# Revit family: ONIZ_5BF
name_source: partatom
category: Mechanical Equipment
units: mm (PartAtom-declared; Revit-internal decimal feet)

## family parameters
Always vertical = Yes
Cut with Voids When Loaded = No
OmniClass Number = 23.40.40.11.17
OmniClass Title = Refrigerated Cases
Part Type = Normal
Room Calculation Point = No
Round Connector Dimension = Use Radius
Shared = No
Work Plane-Based = Yes

## types (4) — shared parameters
BASE HEIGHT = 5"
CERTIFICATIONS = NSF 7, UL471, CSA
COIL REFRIGERATION CHARGE = 0.00 lb
CONTROL TYPE = T-STAT
DATE = 03/15/12
DEDICATED CIRCUIT = YES
DEFROST PHASE = 1
DEFROST TIME AND DURATION = 2 @ 60 MIN
DEFROST WATTAGE = 0 W
DIEBOARD HEIGHT = 0"
DISCHARGE AIR TEMPERATURE = 0 °F
DRAIN LINE CONNECTION = Drain Connection
DRAIN LINE DIAMETER = 2"
DRAIN LINE RADIUS = 1"
DRAIN PIPE LENGTH = 0"
DRAIN PIPE TYPE = PVC
DRIP PAN PLUMB TYPE = HARD
Default Elevation = 48"
Description = Narrow Single-Deck Island Merchandiser
ELECTRIC DEFROST = No
ELECTRICAL DEFROST VOLTAGE = 0 V
EQUIPMENT MARK = ONIZ
EVAPORATOR TEMPERATURE = 0 °F
FAN CONNECTOR DESCRIPTION = FAN AND ANTI SWEAT CONNECTOR
FAN NUMBER OF POLES = 1
FAN TYPE = ECM
FROZEN CASE = Yes
GROUND FAULT PROTECTION = NO
HEIGHT = 34 15/16"
HOT GAS DEFROST = No
ISOLATED GROUND REQUIRED = NO
Keynote = Frozen Food/ Ice Cream
LED LIGHTING AMPS = 0 A
LED LIGHTING AMPS PER ROW = 0 A
LED LIGHTING WATTAGE = 0 W
LIGHT AMPS = 0 A
LIGHT TYPE = T8 FLUORESCENT
LIGHTING APPARENT LOAD = 0 VA
LIGHTING CONNECTION DESCRIPTION = LIGHTING CONNECTOR
LIGHTING NUMBER OF POLES = 1
LIGHTING WATTAGE = 0 VA
LIQUID LINE CONNECTION = LIQUID LINE CONNECTION
LIQUID LINE DIAMETER = 0"
LIQUID LINE RADIUS = 0"
Manufacturer = HILL PHOENIX
NUMBER OF WIRES = 3
PHASE = 1
POWER FACTOR = 1
PRESSURE REGULATOR = 0.00 psi
RECEPTICAL MOUNTING HEIGHT ABOVE FLOOR = 19 3/4"
REF PLANE FRONT BACK = 22 1/2"
REVERSE AIR DEFROST = No
SET BACK MODE FOR ENERGY CONSERVATION = NO
SHELVE LENGTH = 48"
SIZE OF COLD WATER HOOK UP = 0"
SIZE OF HOT WATER HOOK-UP = 0"
SUCTION LINE CONNECTION = SUCTION LINE CONNECTION
SUCTION LINE DIAMETER = 1"
SUCTION LINE RADIUS = 0"
T8 LIGHT OR LED LIGHT = Yes
T8 LIGHTING AMPS = 0 A
T8 LIGHTING AMPS PER ROW = 0 A
T8 LIGHTING WATTAGE = 0 W
TIME OFF DEFROST = Yes
TOEKICK HEIGHT = 5 1/2"
TOEKICK INSET = 1 1/2"
URL = http://www.hillphoenix.com
VOLTAGE = 120 V
WATER LINE MOUNTING HEIGHT ABOVE FLOOR = 0"
WEIGHT = 0.00 lb
WIDTH = 45"
zero-valued in all types: BTU ADD FOR LIGHTS, BTU ADD PER SHELF PER FOOT, BTU PER FOOT CONVENTIONAL, BTU PER FOOT PARALLEL, CONVENTIONAL EVAPORATOR LOAD, CORNICE AND NOSE LIGHT ROWS, LED LIGHTING BTU ADD PER ROW, PARALLEL EVAPORATOR LOAD, SHELF LIGHT ROWS, T8 LIGHTING BTU ADD PER ROW

## per-type parameters (varying)
| type | ANTI SWEAT APPARENT LOAD | ANTI SWEAT HEATER AMPS | ANTI SWEAT HEATER WATTAGE | C CASE DEFROST AMPS | DEFROST AMPS | F CASE DEFROST AMPS | FAN AMPS | FAN AND ANTI SWEAT HEATER APPARENT LOAD | FAN APPARENT LOAD | FAN QUANTITY | FAN WATTAGE | LENGTH | LENGTH FOR BTU | REF PLANE LEFT RIGHT | TOTAL APPARENT FAN-LIGHT AND A/S LOAD | TOTAL CASE AMPS | TOTAL CASE WATTAGE |
| ONIZ-8' | 157 VA | 1 A | 157 W | 15 A | 8 A | 8 A | 0 A | 211 VA | 54 VA | 3 | 33 W | 96" | 8 | 48" | 190 VA | 2 A | 190 W |
| ONIZ-12' | 238 VA | 2 A | 238 W | 23 A | 12 A | 12 A | 1 A | 310 VA | 72 VA | 4 | 44 W | 144" | 12 | 72" | 282 VA | 3 A | 282 W |
| ONIZ-6' | 134 VA | 1 A | 134 W | 12 A | 6 A | 6 A | 0 A | 170 VA | 36 VA | 2 | 22 W | 72" | 6 | 36" | 156 VA | 1 A | 156 W |
| ONIZ-10' | 192 VA | 2 A | 192 W | 16 A | 10 A | 10 A | 0 A | 246 VA | 54 VA | 3 | 33 W | 120" | 10 | 60" | 225 VA | 2 A | 225 W |

note: column(s) folded — value = type name in every type: LEGEND NUMBER, Model

## geometry (parser evidence)
native form markers: Blend x2, Sweep x8
no freeform markers — native parametric forms only
